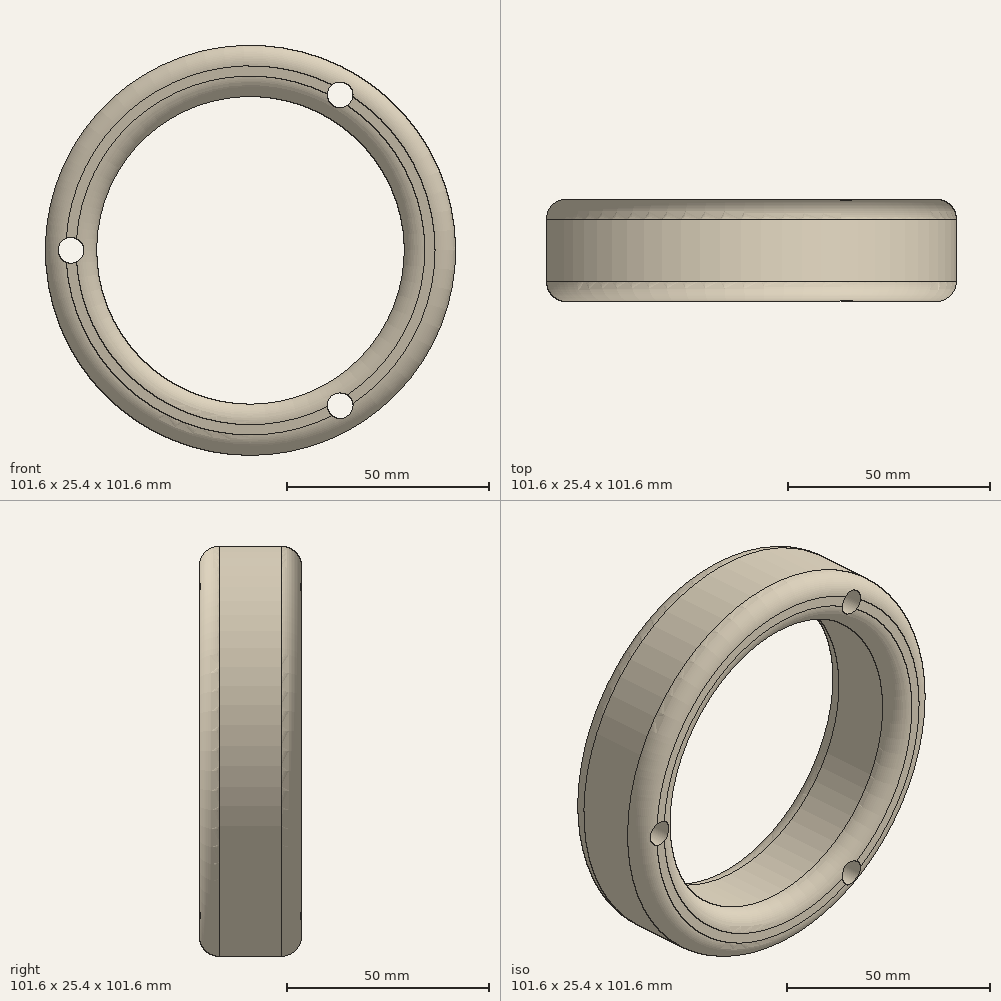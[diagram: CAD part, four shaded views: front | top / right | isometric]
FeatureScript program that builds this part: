
annotation { "Feature Type Name" : "Feature", "Feature Type Description" : "" }
export const myFeature = defineFeature(function(context is Context, id is Id, definition is map)
    precondition{}
    {
        {
            var Q0;
            Q0=qCreatedBy(makeId("Front.planeOp"),FACE);
            var sketch = newSketch(context, id + "F0", { "sketchPlane" : qUnion([Q0])});
            skCircle(sketch, "E0", {"center": v(0, 0) * mm, "radius": 38.1 * mm});
            skCircle(sketch, "E1", {"center": v(0, 0) * mm, "radius": 50.8 * mm});
            skCircle(sketch, "E2", {"center": v(-44.45, 0) * mm, "radius": 3.18 * mm});
            skLineSegment(sketch, "E3.anchor1", {"start": v(0, 0) * mm, "end": v(-44.45, 0) * mm, "construction": true});
            skLineSegment(sketch, "E3.anchor2", {"start": v(0, 0) * mm, "end": v(-44.45, 0) * mm, "construction": true});
            skCircle(sketch, "E4.1.0", {"center": v(22.22, -38.5) * mm, "radius": 3.18 * mm});
            skCircle(sketch, "E4.2.0", {"center": v(22.23, 38.5) * mm, "radius": 3.18 * mm});
            skSolve(sketch);
        }
        {
            var Q0;
            Q0 = qSketchRegion(id + "F0", true);
            extrude(context, id + "F1", {"entities" : qUnion([Q0]), "depth" : 25.4 * mm, "offsetDistance" : 25.4 * mm});
        }
        {
            var Q0;
            Q0=makeQuery(id+"F1.opExtrude","CAP_EDGE",EDGE,{"disambiguationData":[OSD([sQuery(id+"F0.wireOp",EDGE,"E1")])],"isStart":true});
            var Q1;
            Q1=makeQuery(id+"F1.opExtrude","CAP_EDGE",EDGE,{"disambiguationData":[OSD([sQuery(id+"F0.wireOp",EDGE,"E0")])],"isStart":true});
            var Q2;
            Q2=makeQuery(id+"F1.opExtrude","CAP_EDGE",EDGE,{"disambiguationData":[OSD([sQuery(id+"F0.wireOp",EDGE,"E0")])],"isStart":false});
            var Q3;
            Q3=makeQuery(id+"F1.opExtrude","CAP_EDGE",EDGE,{"disambiguationData":[OSD([sQuery(id+"F0.wireOp",EDGE,"E1")])],"isStart":false});
            fillet(context, id + "F2", {"entities" : qUnion([Q0, Q1, Q2, Q3]), "radius" : 5.08 * mm, "tangentPropagation" : true, "allowEdgeOverflow" : false});
        }
    });
